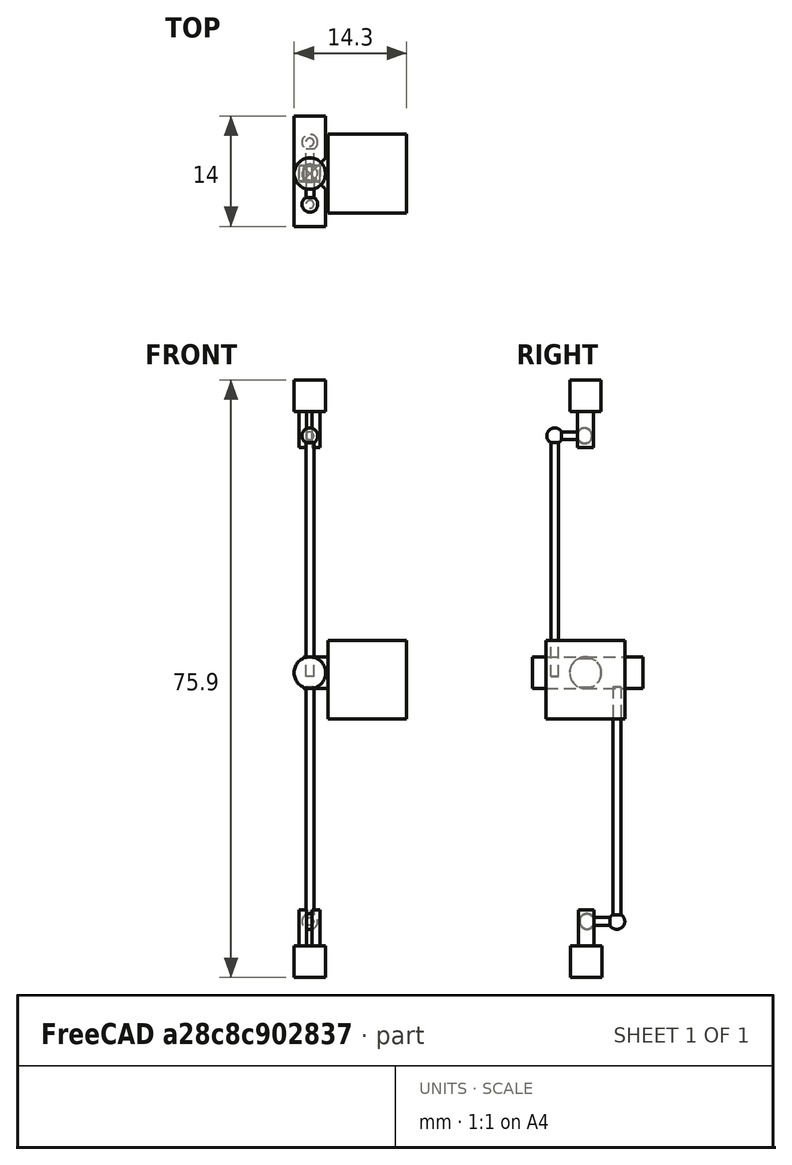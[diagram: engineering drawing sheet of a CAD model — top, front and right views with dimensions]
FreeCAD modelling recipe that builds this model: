
FCSTD DOCUMENT  (FreeCAD 0.18R4 (GitTag))
Label: Direccion Reto
License: All rights reserved
LicenseURL: http://en.wikipedia.org/wiki/All_rights_reserved
objects: Part::Cylinder×10, Part::MultiFuse×9, Part::Box×5, Part::Sphere×4
note: 28 computed .brp shape members not serialized (recipe doc carries the construction recipe); baked Part::Feature solids carry a one-line shape summary decoded from their .brp

FEATURE [Part::Cylinder] Cylinder  label="Cilindro"
  Angle = 360
  AttacherType = Attacher::AttachEngine3D
  Height = 4
  Radius = 1.99
FEATURE [Part::Box] Box001  label="Cubo001"
  AttacherType = Attacher::AttachEngine3D
  Height = 2
  Length = 1
  Placement = pos=(-1.4,-1,0.4) rot=(1,0,0;4.71239rad)
  Width = 5
FEATURE [Part::Box] Box002  label="Cubo002"
  AttacherType = Attacher::AttachEngine3D
  Height = 2
  Length = 1
  Placement = pos=(0.3,-1,0.4) rot=(-1,0,0;1.5708rad)
  Width = 5
FEATURE [Part::MultiFuse] Fusion
  Refine = true
  Shapes = -> [Box002,Box001,Cylinder]
FEATURE [Part::Cylinder] Cylinder001  label="Cilindro001"
  Angle = 360
  AttacherType = Attacher::AttachEngine3D
  Height = 2
  Placement = pos=(-0.9,0,-3.1) rot=(0,1,0;1.5708rad)
  Radius = 0.5
FEATURE [Part::MultiFuse] Fusion001
  Refine = true
  Shapes = -> [Cylinder001,Fusion]
FEATURE [Part::Cylinder] Cylinder002  label="Cilindro002"
  Angle = 360
  AttacherType = Attacher::AttachEngine3D
  Height = 4
  Placement = pos=(0,-1.3e-15,-3.1) rot=(-1,0,0;4.71239rad)
  Radius = 0.5
FEATURE [Part::MultiFuse] Fusion002
  Refine = true
  Shapes = -> [Cylinder002,Fusion001]
FEATURE [Part::Sphere] Sphere  label="Esfera"
  Angle1 = -90
  Angle2 = 90
  Angle3 = 360
  AttacherType = Attacher::AttachEngine3D
  Placement = pos=(0,-0.1,-3.1) rot=(0,0,1;0rad)
  Radius = 1
FEATURE [Part::Sphere] Sphere001  label="Esfera001"
  Angle1 = -90
  Angle2 = 90
  Angle3 = 360
  AttacherType = Attacher::AttachEngine3D
  Placement = pos=(0,-3.9,-3.1) rot=(0,0,1;0rad)
  Radius = 1
FEATURE [Part::Cylinder] Cylinder003  label="Cilindro003"
  Angle = 360
  AttacherType = Attacher::AttachEngine3D
  Height = 30
  Placement = pos=(0,-3.9,-33.7) rot=(0,0,1;0rad)
  Radius = 0.5
FEATURE [Part::MultiFuse] Fusion003
  Refine = true
  Shapes = -> [Cylinder003,Sphere001,Sphere,Fusion002]
FEATURE [Part::Cylinder] Cylinder004  label="Cilindro004"
  Angle = 360
  AttacherType = Attacher::AttachEngine3D
  Height = 30
  Placement = pos=(0,-3.9,-32.9) rot=(0,0,1;0rad)
  Radius = 0.5
FEATURE [Part::Box] Box003  label="Cubo003"
  AttacherType = Attacher::AttachEngine3D
  Height = 2
  Length = 1
  Placement = pos=(-1.4,-1,0.4) rot=(-1,0,0;1.5708rad)
  Width = 5
FEATURE [Part::Box] Box004  label="Cubo004"
  AttacherType = Attacher::AttachEngine3D
  Height = 2
  Length = 1
  Placement = pos=(0.3,-1,0.4) rot=(-1,0,0;1.5708rad)
  Width = 5
FEATURE [Part::Cylinder] Cylinder005  label="Cilindro005"
  Angle = 360
  AttacherType = Attacher::AttachEngine3D
  Height = 4
  Radius = 1.99
FEATURE [Part::Cylinder] Cylinder006  label="Cilindro006"
  Angle = 360
  AttacherType = Attacher::AttachEngine3D
  Height = 2
  Placement = pos=(-0.9,0,-3.1) rot=(0,1,0;1.5708rad)
  Radius = 0.5
FEATURE [Part::Cylinder] Cylinder007  label="Cilindro007"
  Angle = 360
  AttacherType = Attacher::AttachEngine3D
  Height = 4
  Placement = pos=(0,-1e-15,-3.1) rot=(1,0,0;1.5708rad)
  Radius = 0.5
FEATURE [Part::MultiFuse] Fusion004
  Refine = true
  Shapes = -> [Box004,Box003,Cylinder005]
FEATURE [Part::MultiFuse] Fusion005
  Refine = true
  Shapes = -> [Cylinder006,Fusion004]
FEATURE [Part::MultiFuse] Fusion007
  Refine = true
  Shapes = -> [Cylinder007,Fusion005]
FEATURE [Part::Sphere] Sphere002  label="Esfera002"
  Angle1 = -90
  Angle2 = 90
  Angle3 = 360
  AttacherType = Attacher::AttachEngine3D
  Placement = pos=(0,-0.1,-3.1) rot=(0,0,1;0rad)
  Radius = 1
FEATURE [Part::Sphere] Sphere003  label="Esfera003"
  Angle1 = -90
  Angle2 = 90
  Angle3 = 360
  AttacherType = Attacher::AttachEngine3D
  Placement = pos=(0,-3.9,-3.1) rot=(0,0,1;0rad)
  Radius = 1
FEATURE [Part::MultiFuse] Fusion006
  Placement = pos=(0,0.1,-67.9) rot=(1,0,0;3.14159rad)
  Refine = true
  Shapes = -> [Cylinder004,Sphere003,Sphere002,Fusion007]
FEATURE [Part::Box] Box  label="Cubo"
  AttacherType = Attacher::AttachEngine3D
  Height = 10
  Length = 10
  Placement = pos=(2.3,-4,-39.1) rot=(0,0,1;0rad)
  Width = 10
FEATURE [Part::Cylinder] Cylinder008  label="Cilindro008"
  Angle = 360
  AttacherType = Attacher::AttachEngine3D
  Height = 10
  Placement = pos=(9.2,1,-33.2) rot=(-0.57735,-0.57735,0.57735;2.0944rad)
  Radius = 2
FEATURE [Part::Cylinder] Cylinder009  label="Cilindro009"
  Angle = 360
  AttacherType = Attacher::AttachEngine3D
  Height = 14
  Placement = pos=(0,-5.7,-33.2) rot=(1,0,0;4.71239rad)
  Radius = 2
FEATURE [Part::MultiFuse] Fusion008
  Placement = pos=(0,-1,0) rot=(0,0,1;0rad)
  Refine = true
  Shapes = -> [Cylinder009,Cylinder008,Box]
